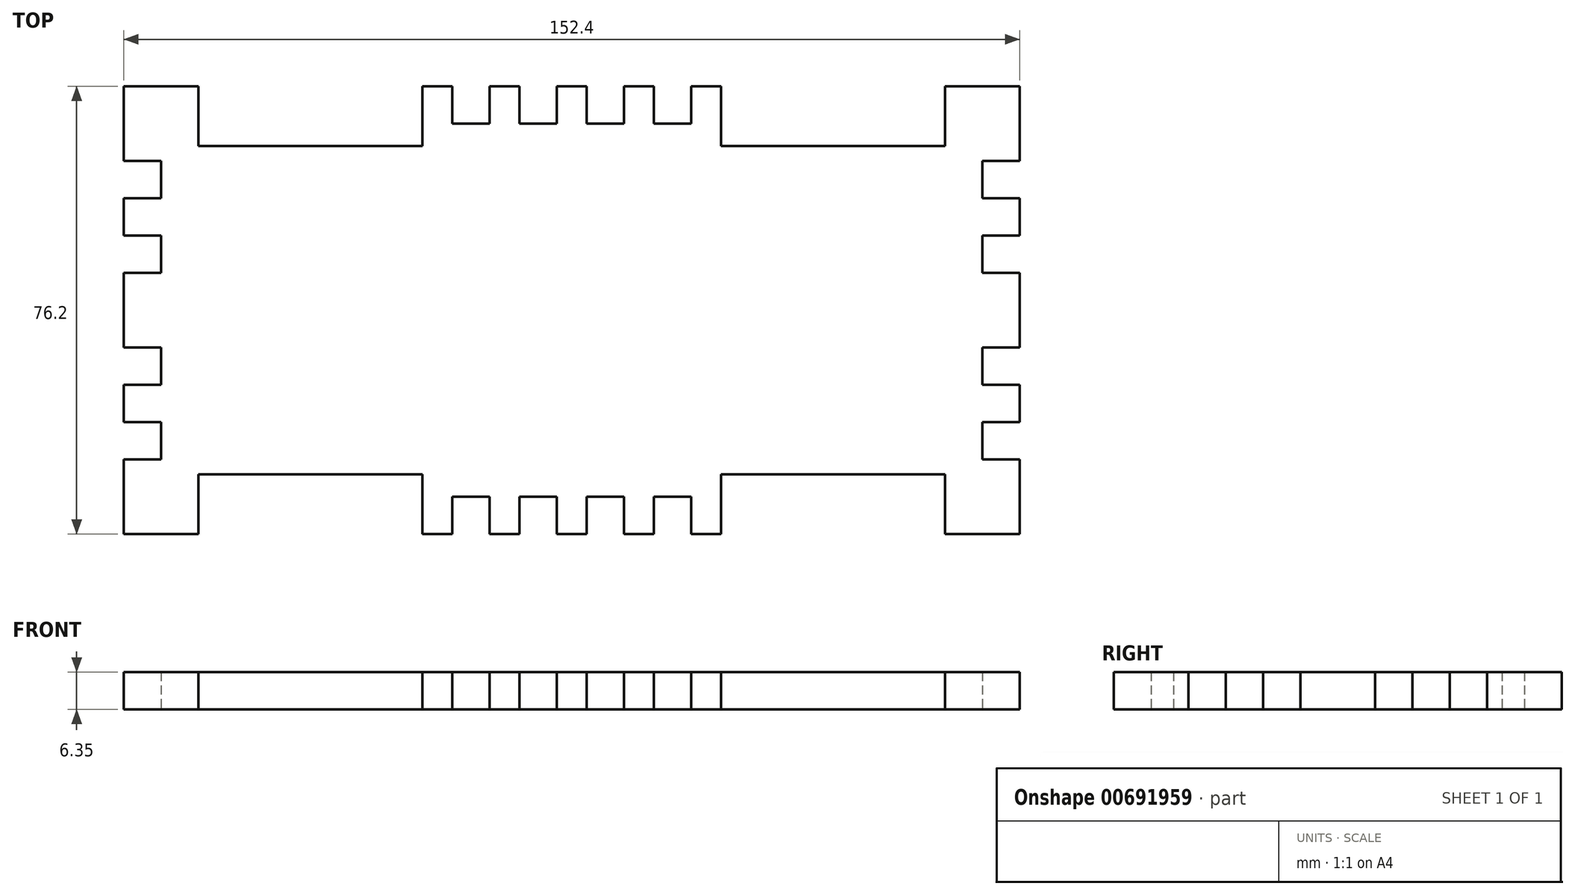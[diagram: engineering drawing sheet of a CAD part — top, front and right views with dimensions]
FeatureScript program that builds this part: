
annotation { "Feature Type Name" : "Feature", "Feature Type Description" : "" }
export const myFeature = defineFeature(function(context is Context, id is Id, definition is map)
    precondition{}
    {
        {
            var Q0;
            Q0=qCreatedBy(makeId("Top.planeOp"),FACE);
            var sketch = newSketch(context, id + "F0", { "sketchPlane" : qUnion([Q0])});
            skLineSegment(sketch, "E0.bottom", {"start": v(76.2, -38.1) * mm, "end": v(-76.2, -38.1) * mm});
            skLineSegment(sketch, "E0.top", {"start": v(76.2, 38.1) * mm, "end": v(-76.2, 38.1) * mm});
            skLineSegment(sketch, "E0.left", {"start": v(76.2, -38.1) * mm, "end": v(76.2, 38.1) * mm});
            skLineSegment(sketch, "E0.right", {"start": v(-76.2, -38.1) * mm, "end": v(-76.2, 38.1) * mm});
            skPoint(sketch, "E0.middle", {"position": v(0, 0) * mm});
            skLineSegment(sketch, "E1", {"start": v(-76.2, 0) * mm, "end": v(76.2, 0) * mm});
            skLineSegment(sketch, "E2.bottom", {"start": v(-63.5, -38.1) * mm, "end": v(-25.4, -38.1) * mm});
            skLineSegment(sketch, "E2.top", {"start": v(-63.5, -27.94) * mm, "end": v(-25.4, -27.94) * mm});
            skLineSegment(sketch, "E2.left", {"start": v(-63.5, -38.1) * mm, "end": v(-63.5, -27.94) * mm});
            skLineSegment(sketch, "E2.right", {"start": v(-25.4, -38.1) * mm, "end": v(-25.4, -27.94) * mm});
            skLineSegment(sketch, "E3", {"start": v(0, 38.1) * mm, "end": v(0, -38.1) * mm});
            skLineSegment(sketch, "E4.MirrorCS", {"start": v(63.5, -38.1) * mm, "end": v(63.5, -27.94) * mm});
            skLineSegment(sketch, "E5.MirrorCS", {"start": v(63.5, -27.94) * mm, "end": v(25.4, -27.94) * mm});
            skLineSegment(sketch, "E6.MirrorCS", {"start": v(25.4, -38.1) * mm, "end": v(25.4, -27.94) * mm});
            skLineSegment(sketch, "E7.bottom", {"start": v(-20.32, -38.1) * mm, "end": v(-13.97, -38.1) * mm});
            skLineSegment(sketch, "E7.top", {"start": v(-20.32, -31.75) * mm, "end": v(-13.97, -31.75) * mm});
            skLineSegment(sketch, "E7.left", {"start": v(-20.32, -38.1) * mm, "end": v(-20.32, -31.75) * mm});
            skLineSegment(sketch, "E7.right", {"start": v(-13.97, -38.1) * mm, "end": v(-13.97, -31.75) * mm});
            skLineSegment(sketch, "E8.direction1", {"start": v(-20.32, -38.1) * mm, "end": v(0, -38.1) * mm, "construction": true});
            skLineSegment(sketch, "E9.MirrorCS", {"start": v(20.32, -38.1) * mm, "end": v(20.32, -31.75) * mm});
            skLineSegment(sketch, "E10.MirrorCS", {"start": v(20.32, -31.75) * mm, "end": v(13.97, -31.75) * mm});
            skLineSegment(sketch, "E11.MirrorCS", {"start": v(13.97, -38.1) * mm, "end": v(13.97, -31.75) * mm});
            skLineSegment(sketch, "E12.MirrorCS", {"start": v(20.32, 31.75) * mm, "end": v(13.97, 31.75) * mm});
            skLineSegment(sketch, "E13.MirrorCS", {"start": v(-63.5, 27.94) * mm, "end": v(-25.4, 27.94) * mm});
            skLineSegment(sketch, "E14.MirrorCS", {"start": v(63.5, 27.94) * mm, "end": v(25.4, 27.94) * mm});
            skLineSegment(sketch, "E15.MirrorCS", {"start": v(-20.32, 31.75) * mm, "end": v(-13.97, 31.75) * mm});
            skLineSegment(sketch, "E16.MirrorCS", {"start": v(-20.32, 38.1) * mm, "end": v(-13.97, 38.1) * mm});
            skLineSegment(sketch, "E17.MirrorCS", {"start": v(13.97, 38.1) * mm, "end": v(13.97, 31.75) * mm});
            skLineSegment(sketch, "E18.MirrorCS", {"start": v(-63.5, 38.1) * mm, "end": v(-63.5, 27.94) * mm});
            skLineSegment(sketch, "E19.MirrorCS", {"start": v(-25.4, 38.1) * mm, "end": v(-25.4, 27.94) * mm});
            skLineSegment(sketch, "E20.MirrorCS", {"start": v(63.5, 38.1) * mm, "end": v(63.5, 27.94) * mm});
            skLineSegment(sketch, "E21.MirrorCS", {"start": v(-13.97, 38.1) * mm, "end": v(-13.97, 31.75) * mm});
            skLineSegment(sketch, "E22.MirrorCS", {"start": v(-20.32, 38.1) * mm, "end": v(-20.32, 31.75) * mm});
            skLineSegment(sketch, "E23.MirrorCS", {"start": v(25.4, 38.1) * mm, "end": v(25.4, 27.94) * mm});
            skLineSegment(sketch, "E24.MirrorCS", {"start": v(-63.5, 38.1) * mm, "end": v(-25.4, 38.1) * mm});
            skLineSegment(sketch, "E25.MirrorCS", {"start": v(20.32, 38.1) * mm, "end": v(20.32, 31.75) * mm});
            skLineSegment(sketch, "E26.MirrorCS", {"start": v(-20.32, 38.1) * mm, "end": v(0, 38.1) * mm, "construction": true});
            skLineSegment(sketch, "E27.1.0.0", {"start": v(-8.9, -38.1) * mm, "end": v(-8.9, -31.75) * mm});
            skLineSegment(sketch, "E27.1.0.1", {"start": v(-8.9, -31.75) * mm, "end": v(-2.54, -31.75) * mm});
            skLineSegment(sketch, "E27.1.0.2", {"start": v(-2.54, -38.1) * mm, "end": v(-2.54, -31.75) * mm});
            skLineSegment(sketch, "E27.direction1", {"start": v(-20.32, -38.1) * mm, "end": v(-8.9, -38.1) * mm, "construction": true});
            skLineSegment(sketch, "E28.MirrorCS", {"start": v(8.9, -31.75) * mm, "end": v(2.54, -31.75) * mm});
            skLineSegment(sketch, "E29.MirrorCS", {"start": v(8.9, -38.1) * mm, "end": v(8.9, -31.75) * mm});
            skLineSegment(sketch, "E30.MirrorCS", {"start": v(2.54, -38.1) * mm, "end": v(2.54, -31.75) * mm});
            skLineSegment(sketch, "E31.MirrorCS", {"start": v(-8.9, 31.75) * mm, "end": v(-2.54, 31.75) * mm});
            skLineSegment(sketch, "E32.MirrorCS", {"start": v(-8.89, 38.1) * mm, "end": v(-8.89, 31.75) * mm});
            skLineSegment(sketch, "E33.MirrorCS", {"start": v(-2.54, 38.1) * mm, "end": v(-2.54, 31.75) * mm});
            skLineSegment(sketch, "E34.MirrorCS", {"start": v(8.9, 31.75) * mm, "end": v(2.54, 31.75) * mm});
            skLineSegment(sketch, "E35.MirrorCS", {"start": v(2.54, 38.1) * mm, "end": v(2.54, 31.75) * mm});
            skLineSegment(sketch, "E36.MirrorCS", {"start": v(8.89, 38.1) * mm, "end": v(8.89, 31.75) * mm});
            skLineSegment(sketch, "E37.bottom", {"start": v(-76.2, 25.4) * mm, "end": v(-69.85, 25.4) * mm});
            skLineSegment(sketch, "E37.top", {"start": v(-76.2, 19.05) * mm, "end": v(-69.85, 19.05) * mm});
            skLineSegment(sketch, "E37.left", {"start": v(-76.2, 25.4) * mm, "end": v(-76.2, 19.05) * mm});
            skLineSegment(sketch, "E37.right", {"start": v(-69.85, 25.4) * mm, "end": v(-69.85, 19.05) * mm});
            skLineSegment(sketch, "E38.1.0.0", {"start": v(-76.2, 12.7) * mm, "end": v(-69.85, 12.7) * mm});
            skLineSegment(sketch, "E38.1.0.1", {"start": v(-69.85, 12.7) * mm, "end": v(-69.85, 6.35) * mm});
            skLineSegment(sketch, "E38.1.0.2", {"start": v(-76.2, 6.35) * mm, "end": v(-69.85, 6.35) * mm});
            skLineSegment(sketch, "E38.direction1", {"start": v(-76.2, 25.4) * mm, "end": v(-76.2, 12.7) * mm, "construction": true});
            skLineSegment(sketch, "E39.MirrorCS", {"start": v(-76.2, -25.4) * mm, "end": v(-76.2, -19.05) * mm});
            skLineSegment(sketch, "E40.MirrorCS", {"start": v(-76.2, -12.7) * mm, "end": v(-69.85, -12.7) * mm});
            skLineSegment(sketch, "E41.MirrorCS", {"start": v(-76.2, 38.1) * mm, "end": v(-76.2, -38.1) * mm});
            skLineSegment(sketch, "E42.MirrorCS", {"start": v(-76.2, -6.35) * mm, "end": v(-69.85, -6.35) * mm});
            skLineSegment(sketch, "E43.MirrorCS", {"start": v(-76.2, -19.05) * mm, "end": v(-69.85, -19.05) * mm});
            skLineSegment(sketch, "E44.MirrorCS", {"start": v(-69.85, -12.7) * mm, "end": v(-69.85, -6.35) * mm});
            skLineSegment(sketch, "E45.MirrorCS", {"start": v(-76.2, -25.4) * mm, "end": v(-76.2, -12.7) * mm, "construction": true});
            skLineSegment(sketch, "E46.MirrorCS", {"start": v(-76.2, -25.4) * mm, "end": v(-69.85, -25.4) * mm});
            skLineSegment(sketch, "E47.MirrorCS", {"start": v(-69.85, -25.4) * mm, "end": v(-69.85, -19.05) * mm});
            skLineSegment(sketch, "E48.MirrorCS", {"start": v(76.2, -25.4) * mm, "end": v(76.2, -19.05) * mm});
            skLineSegment(sketch, "E49.MirrorCS", {"start": v(76.2, 38.1) * mm, "end": v(76.2, -38.1) * mm});
            skLineSegment(sketch, "E50.MirrorCS", {"start": v(76.2, 25.4) * mm, "end": v(76.2, 19.05) * mm});
            skLineSegment(sketch, "E51.MirrorCS", {"start": v(69.85, 25.4) * mm, "end": v(69.85, 19.05) * mm});
            skLineSegment(sketch, "E52.MirrorCS", {"start": v(76.2, -25.4) * mm, "end": v(76.2, -12.7) * mm, "construction": true});
            skLineSegment(sketch, "E53.MirrorCS", {"start": v(76.2, 6.35) * mm, "end": v(69.85, 6.35) * mm});
            skLineSegment(sketch, "E54.MirrorCS", {"start": v(76.2, -19.05) * mm, "end": v(69.85, -19.05) * mm});
            skLineSegment(sketch, "E55.MirrorCS", {"start": v(76.2, 25.4) * mm, "end": v(76.2, 12.7) * mm, "construction": true});
            skLineSegment(sketch, "E56.MirrorCS", {"start": v(69.85, -12.7) * mm, "end": v(69.85, -6.35) * mm});
            skLineSegment(sketch, "E57.MirrorCS", {"start": v(76.2, -25.4) * mm, "end": v(69.85, -25.4) * mm});
            skLineSegment(sketch, "E58.MirrorCS", {"start": v(69.85, 12.7) * mm, "end": v(69.85, 6.35) * mm});
            skLineSegment(sketch, "E59.MirrorCS", {"start": v(76.2, 19.05) * mm, "end": v(69.85, 19.05) * mm});
            skLineSegment(sketch, "E60.MirrorCS", {"start": v(76.2, 12.7) * mm, "end": v(69.85, 12.7) * mm});
            skLineSegment(sketch, "E61.MirrorCS", {"start": v(76.2, 25.4) * mm, "end": v(69.85, 25.4) * mm});
            skLineSegment(sketch, "E62.MirrorCS", {"start": v(76.2, -12.7) * mm, "end": v(69.85, -12.7) * mm});
            skLineSegment(sketch, "E63.MirrorCS", {"start": v(69.85, -25.4) * mm, "end": v(69.85, -19.05) * mm});
            skLineSegment(sketch, "E64.MirrorCS", {"start": v(76.2, -6.35) * mm, "end": v(69.85, -6.35) * mm});
            skLineSegment(sketch, "E65.MirrorCS", {"start": v(76.2, 0) * mm, "end": v(-76.2, 0) * mm});
            skSolve(sketch);
        }
        {
            var Q0;
            Q0=makeQuery(id+"F0.imprint","IMPRINT",FACE,{"disambiguationData":[TD([[makeQuery(id+"F0.imprint","IMPRINT",EDGE,{"derivedFrom":sQuery(id+"F0.wireOp",EDGE,"E13.MirrorCS")}),-1.0]])]});
            var Q1;
            Q1=makeQuery(id+"F0.imprint","IMPRINT",FACE,{"disambiguationData":[TD([[makeQuery(id+"F0.imprint","IMPRINT",EDGE,{"derivedFrom":sQuery(id+"F0.wireOp",EDGE,"E2.top")}),1.0]])]});
            var Q2;
            {var subQ4=sQuery(id+"F0.wireOp",EDGE,"E4.MirrorCS");Q2=makeQuery(id+"F0.imprint","IMPRINT",FACE,{"disambiguationData":[TD([[makeQuery(id+"F0.imprint","IMPRINT",EDGE,{"derivedFrom":subQ4}),-1.0]])]});}
            var Q3;
            Q3=makeQuery(id+"F0.imprint","IMPRINT",FACE,{"disambiguationData":[TD([[makeQuery(id+"F0.imprint","IMPRINT",EDGE,{"derivedFrom":sQuery(id+"F0.wireOp",EDGE,"E12.MirrorCS")}),1.0]])]});
            extrude(context, id + "F1", {"entities" : qUnion([Q0, Q1, Q2, Q3]), "depth" : 6.35 * mm, "offsetDistance" : 25.4 * mm});
        }
    });
